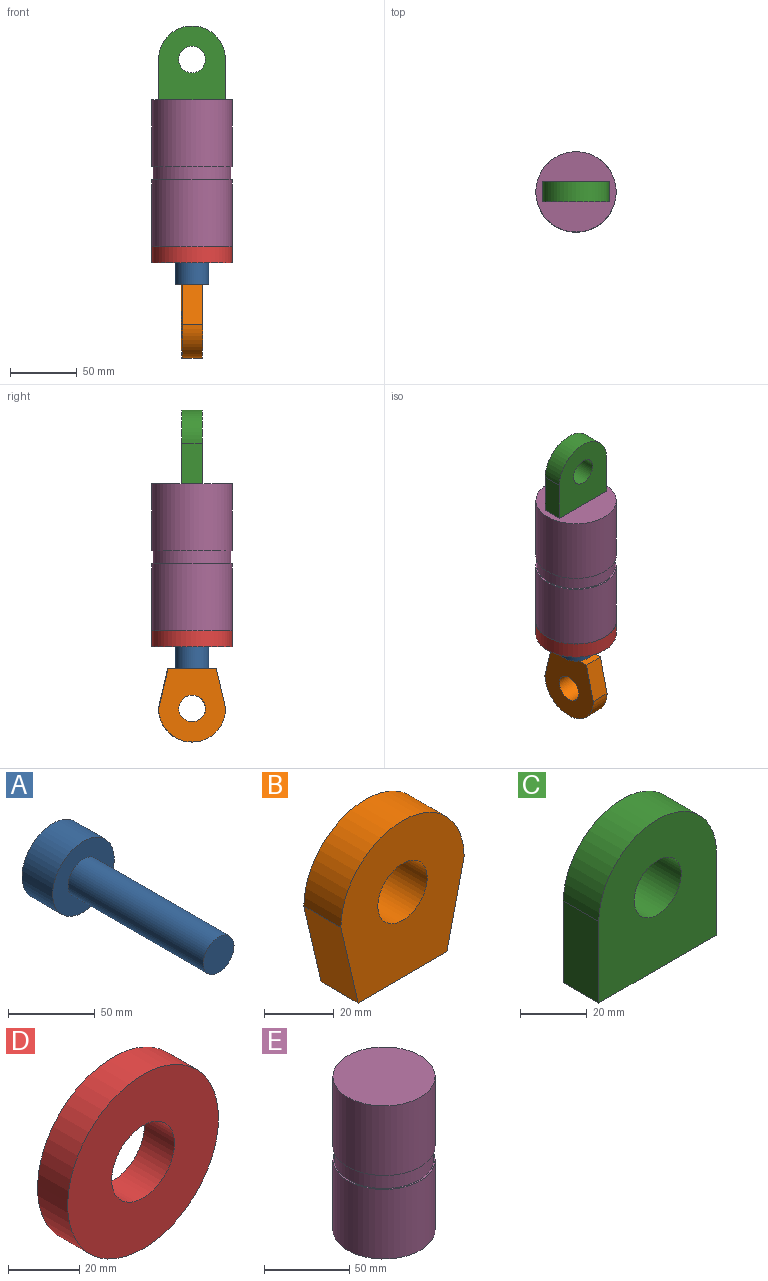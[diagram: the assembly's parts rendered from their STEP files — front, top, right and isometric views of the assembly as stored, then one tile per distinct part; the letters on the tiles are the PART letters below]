
ASSEMBLY  parts=5 mates=4
PART A: 5 faces, bbox 50x135x50 mm
  f0: cylinder r=25mm len=50mm, axis (0,1,0), area 3927mm2, adj f1,f2
  f1: plane 50x50mm, normal (0,-1,0), area 1472.6mm2, adj f0,f3
  f2: plane 50x50mm, normal (0,1,0), area 1963.5mm2, adj f0
  f3: cylinder r=12.5mm len=110mm, axis (0,1,0), area 8639.4mm2, adj f1,f4
  f4: plane 25x25mm, normal (0,-1,0), area 490.9mm2, adj f3
PART B: 7 faces, bbox 50x15x55 mm
  f0: plane 30x15mm, normal (-0.97,0,-0.23), area 462.1mm2, adj f1,f3,f5,f6
  f1: plane 36x15mm, normal (0,0,-1), area 540mm2, adj f0,f2,f5,f6
  f2: plane 30x15mm, normal (0.97,0,-0.23), area 462.1mm2, adj f1,f3,f5,f6
  f3: cylinder r=25mm len=50mm, axis (0,1,0), area 1178.1mm2, adj f0,f2,f5,f6
  f4: cylinder r=10mm len=20mm, axis (0,1,0), area 942.5mm2, adj f5,f6
  f5: plane 55x50mm, normal (0,-1,0), area 1957.6mm2, adj f0,f1,f2,f3,f4
  f6: plane 55x50mm, normal (0,1,0), area 1957.6mm2, adj f0,f1,f2,f3,f4
PART C: 7 faces, bbox 50x15x55 mm
  f0: cylinder r=25mm len=50mm, axis (0,1,0), area 1178.1mm2, adj f1,f4,f5,f6
  f1: plane 30x15mm, normal (-1,0,0), area 450mm2, adj f0,f2,f5,f6
  f2: plane 50x15mm, normal (0,0,-1), area 750mm2, adj f1,f4,f5,f6
  f3: cylinder r=10mm len=20mm, axis (0,1,0), area 942.5mm2, adj f5,f6
  f4: plane 30x15mm, normal (1,0,0), area 450mm2, adj f0,f2,f5,f6
  f5: plane 55x50mm, normal (0,-1,0), area 2167.6mm2, adj f0,f1,f2,f3,f4
  f6: plane 55x50mm, normal (0,1,0), area 2167.6mm2, adj f0,f1,f2,f3,f4
PART D: 4 faces, bbox 60x12x60 mm
  f0: cylinder r=12.5mm len=25mm, axis (0,1,0), area 942.5mm2, adj f2,f3
  f1: cylinder r=30mm len=60mm, axis (0,1,0), area 2261.9mm2, adj f2,f3
  f2: plane 60x60mm, normal (0,-1,0), area 2336.6mm2, adj f0,f1
  f3: plane 60x60mm, normal (0,1,0), area 2336.6mm2, adj f0,f1
PART E: 9 faces, bbox 60x60x110 mm
  f0: cylinder r=30mm len=60mm, axis (0,0,-1), area 9424.8mm2, adj f1,f2
  f1: plane 60x60mm, normal (0,0,1), area 2827.4mm2, adj f0
  f2: plane 60x60mm, normal (0,0,-1), area 185.4mm2, adj f0,f3
  f3: cylinder r=29mm len=58mm, axis (0,0,1), area 1822.1mm2, adj f2,f6
  f4: cylinder r=30mm len=60mm, axis (0,0,1), area 9424.8mm2, adj f5,f6
  f5: plane 60x60mm, normal (0,0,-1), area 863.9mm2, adj f4,f7
  f6: plane 60x60mm, normal (0,0,1), area 185.4mm2, adj f3,f4
  f7: cylinder r=25mm len=105mm, axis (0,0,-1), area 16493.4mm2, adj f5,f8
  f8: plane 50x50mm, normal (0,0,-1), area 1963.5mm2, adj f7
PLACE A rot(axis=(0.59,-0.57,-0.57),119.3deg) t=(-271.72,-156.61,141.29)mm
PLACE B rot(axis=(0.7,0.71,0),180deg) t=(-268.28,-121.96,-18.53)mm
PLACE C t=(-278.16,-113.46,169.7)mm
PLACE D rot(axis=(-1,0,0),90deg) t=(-244.26,-147.86,22.29)mm
PLACE E t=(-326,-152.75,94.29)mm fixed
MATE cylindrical A.f0 <-> E.f0  axis (0,0,1) through (-275.8,-120.96,141.29)mm
MATE fastened D.f0 <-> E.f0  axis (0,0,1) through (-275.8,-120.96,34.29)mm
MATE fastened B.f1 <-> A.f0  axis (0,0,1) through (-275.8,-120.96,6.29)mm
MATE fastened C.f2 <-> E.f0  axis (0,0,-1) through (-275.8,-120.96,144.29)mm
